# Revit family: Bjælke-LBE
name_source: partatom
category: Structural Framing
units: mm (PartAtom-declared; Revit-internal decimal feet)

## family parameters
Always export as geometry = No
Always vertical = Yes
Cut with Voids When Loaded = No
Material for Model Behavior = Other
OmniClass Number = 23.25.30.11.14.14
OmniClass Title = Beams
Section Shape = Not Defined
Shared = No
Show family pre-cut in plan views = Yes

## types (24) — shared parameters
CRH_RFA_TimeStamp_LastRelease = 20230829
Hylde Højde Maks = 400 mm  [stored 1.31234 ft]
Manufacturer = CRH Concrete

## per-type parameters (varying)
| type | Bredde | Bredde 2 | Bredt Element | Hylde Højde | Højde | Konsol Tykkelse | Model |
| LBE 50/40/12 | 500 mm  [stored 1.64042 ft] | 170 mm  [stored 0.557743 ft] | No | 400 mm  [stored 1.31234 ft] | 520 mm  [stored 1.70604 ft] | 120 mm  [stored 0.393701 ft] | LBE |
| LBE 50/32/12 | 500 mm  [stored 1.64042 ft] | 170 mm  [stored 0.557743 ft] | No | 320 mm  [stored 1.04987 ft] | 440 mm  [stored 1.44357 ft] | 120 mm  [stored 0.393701 ft] | LBE |
| LBE 50/27/12 | 500 mm  [stored 1.64042 ft] | 170 mm  [stored 0.557743 ft] | No | 270 mm  [stored 0.885827 ft] | 390 mm  [stored 1.27953 ft] | 120 mm  [stored 0.393701 ft] | LBE |
| LBE 50/22/12 | 500 mm  [stored 1.64042 ft] | 170 mm  [stored 0.557743 ft] | No | 220 mm  [stored 0.721785 ft] | 340 mm  [stored 1.11549 ft] | 120 mm  [stored 0.393701 ft] | LBE |
| LBE 50/40/8 | 500 mm  [stored 1.64042 ft] | 170 mm  [stored 0.557743 ft] | No | 400 mm  [stored 1.31234 ft] | 480 mm  [stored 1.5748 ft] | 80 mm  [stored 0.262467 ft] | LBE |
| LBE 50/32/8 | 500 mm  [stored 1.64042 ft] | 170 mm  [stored 0.557743 ft] | No | 320 mm  [stored 1.04987 ft] | 400 mm  [stored 1.31234 ft] | 80 mm  [stored 0.262467 ft] | LBE |
| LBE 50/27/8 | 500 mm  [stored 1.64042 ft] | 170 mm  [stored 0.557743 ft] | No | 270 mm  [stored 0.885827 ft] | 350 mm  [stored 1.14829 ft] | 80 mm  [stored 0.262467 ft] | LBE |
| LBE 50/22/8 | 500 mm  [stored 1.64042 ft] | 170 mm  [stored 0.557743 ft] | No | 220 mm  [stored 0.721785 ft] | 300 mm | 80 mm  [stored 0.262467 ft] | LBE |
| LBE 50/40/16 | 500 mm  [stored 1.64042 ft] | 170 mm  [stored 0.557743 ft] | No | 400 mm  [stored 1.31234 ft] | 560 mm  [stored 1.83727 ft] | 160 mm  [stored 0.524934 ft] | LBE |
| LBE 50/32/16 | 500 mm  [stored 1.64042 ft] | 170 mm  [stored 0.557743 ft] | No | 320 mm  [stored 1.04987 ft] | 480 mm  [stored 1.5748 ft] | 160 mm  [stored 0.524934 ft] | LBE |
| LBE 50/27/16 | 500 mm  [stored 1.64042 ft] | 170 mm  [stored 0.557743 ft] | No | 270 mm  [stored 0.885827 ft] | 430 mm | 160 mm  [stored 0.524934 ft] | LBE |
| LBE 50/22/16 | 500 mm  [stored 1.64042 ft] | 170 mm  [stored 0.557743 ft] | No | 220 mm  [stored 0.721785 ft] | 380 mm | 160 mm  [stored 0.524934 ft] | LBE |
| LBBE 66/40/16 | 660 mm | 240 mm  [stored 0.787402 ft] | Yes | 400 mm  [stored 1.31234 ft] | 560 mm  [stored 1.83727 ft] | 160 mm  [stored 0.524934 ft] | LBBE |
| LBBE 66/32/16 | 660 mm | 240 mm  [stored 0.787402 ft] | Yes | 320 mm  [stored 1.04987 ft] | 480 mm  [stored 1.5748 ft] | 160 mm  [stored 0.524934 ft] | LBBE |
| LBBE 66/27/16 | 660 mm | 240 mm  [stored 0.787402 ft] | Yes | 270 mm  [stored 0.885827 ft] | 430 mm | 160 mm  [stored 0.524934 ft] | LBBE |
| LBBE 66/22/16 | 660 mm | 240 mm  [stored 0.787402 ft] | Yes | 220 mm  [stored 0.721785 ft] | 380 mm | 160 mm  [stored 0.524934 ft] | LBBE |
| LBBE 66/40/12 | 660 mm | 240 mm  [stored 0.787402 ft] | Yes | 400 mm  [stored 1.31234 ft] | 520 mm  [stored 1.70604 ft] | 120 mm  [stored 0.393701 ft] | LBBE |
| LBBE 66/32/12 | 660 mm | 240 mm  [stored 0.787402 ft] | Yes | 320 mm  [stored 1.04987 ft] | 440 mm  [stored 1.44357 ft] | 120 mm  [stored 0.393701 ft] | LBBE |
| LBBE 66/27/12 | 660 mm | 240 mm  [stored 0.787402 ft] | Yes | 270 mm  [stored 0.885827 ft] | 390 mm  [stored 1.27953 ft] | 120 mm  [stored 0.393701 ft] | LBBE |
| LBBE 66/22/12 | 660 mm | 240 mm  [stored 0.787402 ft] | Yes | 220 mm  [stored 0.721785 ft] | 340 mm  [stored 1.11549 ft] | 120 mm  [stored 0.393701 ft] | LBBE |
| LBBE 66/40/8 | 660 mm | 240 mm  [stored 0.787402 ft] | Yes | 400 mm  [stored 1.31234 ft] | 480 mm  [stored 1.5748 ft] | 80 mm  [stored 0.262467 ft] | LBBE |
| LBBE 66/32/8 | 660 mm | 240 mm  [stored 0.787402 ft] | Yes | 320 mm  [stored 1.04987 ft] | 400 mm  [stored 1.31234 ft] | 80 mm  [stored 0.262467 ft] | LBBE |
| LBBE 66/27/8 | 660 mm | 240 mm  [stored 0.787402 ft] | Yes | 270 mm  [stored 0.885827 ft] | 350 mm  [stored 1.14829 ft] | 80 mm  [stored 0.262467 ft] | LBBE |
| LBBE 66/22/8 | 660 mm | 240 mm  [stored 0.787402 ft] | Yes | 220 mm  [stored 0.721785 ft] | 300 mm | 80 mm  [stored 0.262467 ft] | LBBE |

note: [stored X ft] marks values corroborated as IEEE doubles in the binary element streams (Revit-internal decimal feet)

## geometry (parser evidence)
native form markers: Sweep x3
no freeform markers — native parametric forms only
